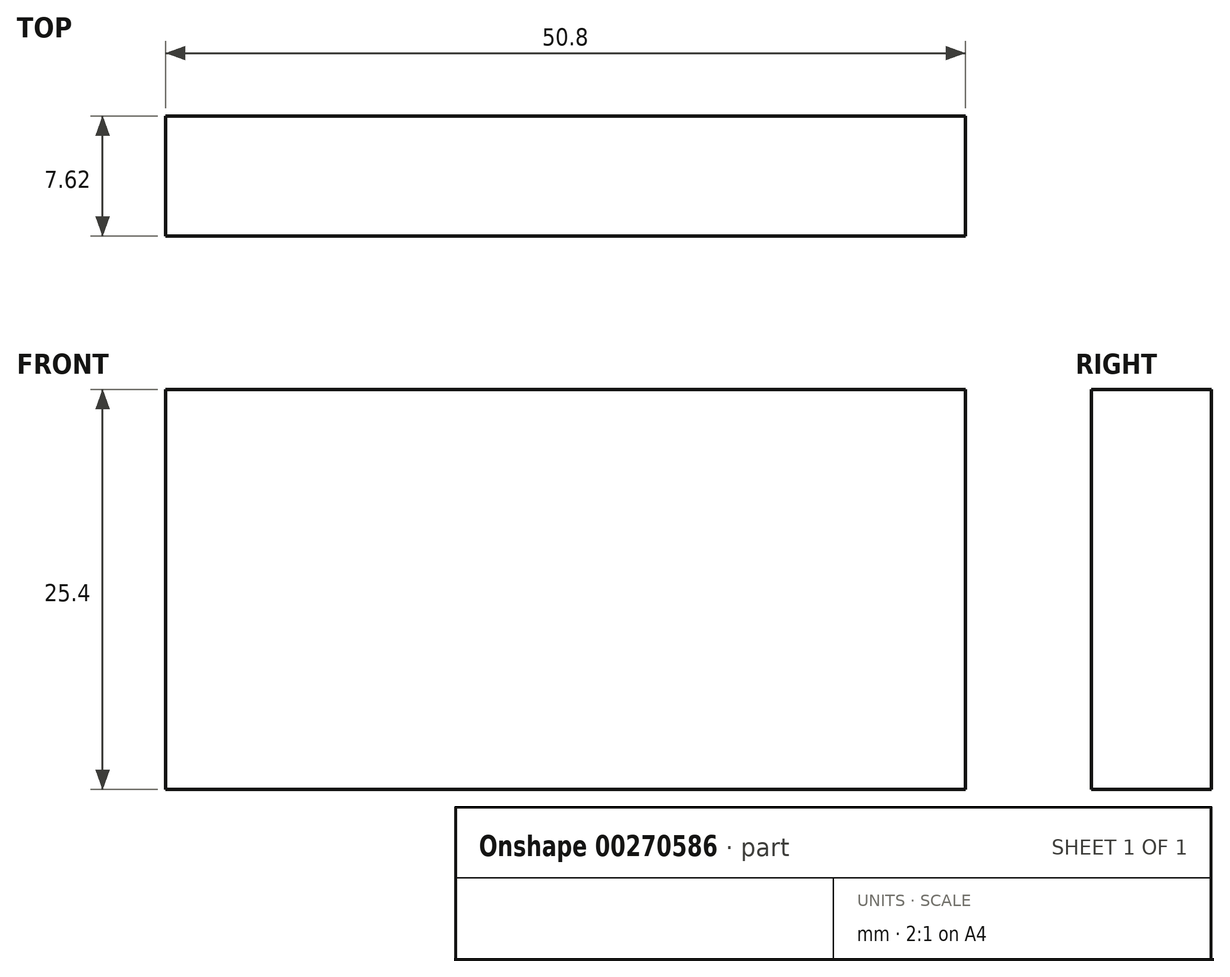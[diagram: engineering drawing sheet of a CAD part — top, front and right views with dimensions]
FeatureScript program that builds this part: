
annotation { "Feature Type Name" : "Feature", "Feature Type Description" : "" }
export const myFeature = defineFeature(function(context is Context, id is Id, definition is map)
    precondition{}
    {
        {
            var Q0;
            Q0=qCreatedBy(makeId("Top.planeOp"),FACE);
            var sketch = newSketch(context, id + "F0", { "sketchPlane" : qUnion([Q0])});
            skLineSegment(sketch, "E0.bottom", {"start": v(25.4, -3.8) * mm, "end": v(-25.4, -3.81) * mm});
            skLineSegment(sketch, "E0.top", {"start": v(25.4, 3.81) * mm, "end": v(-25.4, 3.8) * mm});
            skLineSegment(sketch, "E0.left", {"start": v(25.4, -3.8) * mm, "end": v(25.4, 3.81) * mm});
            skLineSegment(sketch, "E0.right", {"start": v(-25.4, -3.81) * mm, "end": v(-25.4, 3.8) * mm});
            skPoint(sketch, "E0.middle", {"position": v(0, 0) * mm});
            skSolve(sketch);
        }
        {
            var Q0;
            Q0=makeQuery(id+"F0.imprint","IMPRINT",FACE,{"disambiguationData":[TD([[makeQuery(id+"F0.imprint","IMPRINT",EDGE,{"derivedFrom":sQuery(id+"F0.wireOp",EDGE,"E0.bottom")}),-1.0]])]});
            extrude(context, id + "F1", {"entities" : qUnion([Q0]), "depth" : 25.4 * mm});
        }
    });
